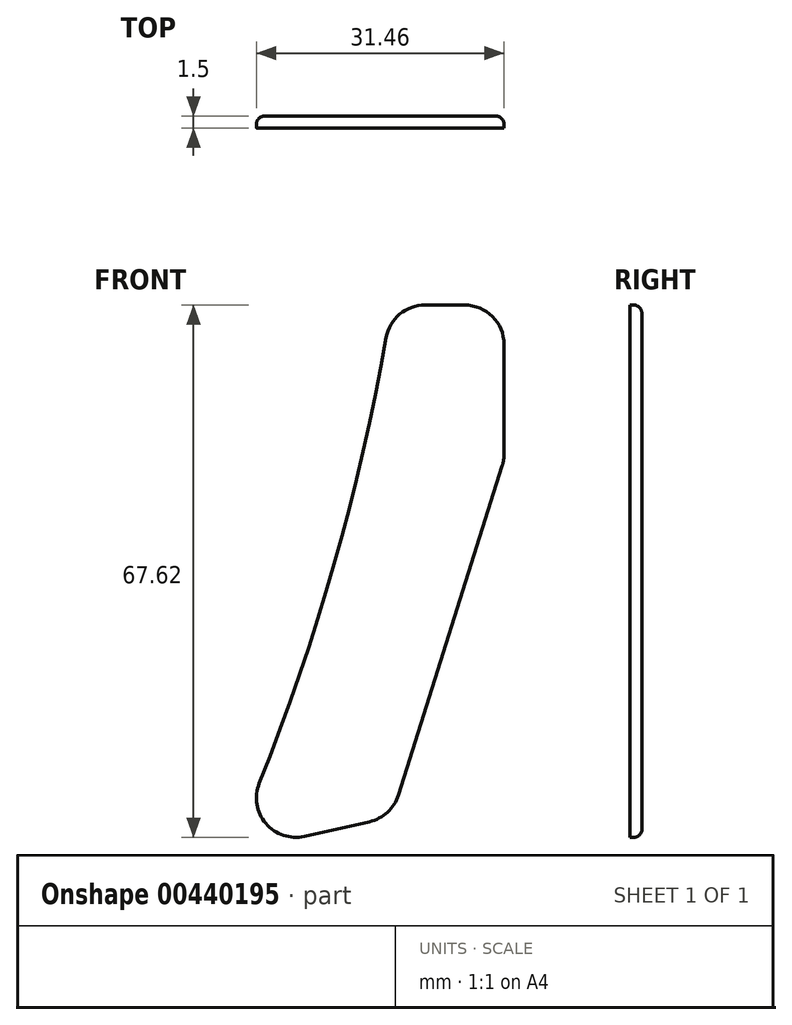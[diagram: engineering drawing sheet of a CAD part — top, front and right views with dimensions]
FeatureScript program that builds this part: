
annotation { "Feature Type Name" : "Feature", "Feature Type Description" : "" }
export const myFeature = defineFeature(function(context is Context, id is Id, definition is map)
    precondition{}
    {
        {
            var Q0;
            Q0=qCreatedBy(makeId("Front.planeOp"),FACE);
            var sketch = newSketch(context, id + "F0", { "sketchPlane" : qUnion([Q0])});
            skLineSegment(sketch, "E0", {"start": v(0, 0) * mm, "end": v(14.28, 0) * mm});
            skLineSegment(sketch, "E1", {"start": v(14.28, 0) * mm, "end": v(14.28, -19.7) * mm});
            skLineSegment(sketch, "E2", {"start": v(14.28, -19.7) * mm, "end": v(0, -65) * mm});
            skLineSegment(sketch, "E3", {"start": v(0, -65) * mm, "end": v(-20.55, -69.63) * mm});
            skLineSegment(sketch, "E4", {"start": v(-20.55, -69.63) * mm, "end": v(-0.94, -2.41) * mm});
            skArc(sketch, "E5", {"start": v(-20.55, -69.63) * mm, "mid": v(-8.05, -35.47) * mm, "end": v(0, 0) * mm});
            skPoint(sketch, "E5.midSnap0", {"position": v(7.14, -42.35) * mm});
            skPoint(sketch, "E5.midSnap1", {"position": v(-10.74, -36.02) * mm});
            skSolve(sketch);
        }
        {
            var Q0;
            Q0 = qSketchRegion(id + "F0", true);
            extrude(context, id + "F1", {"entities" : qUnion([Q0]), "depth" : 1.5 * mm});
        }
        {
            var Q0;
            Q0=makeQuery(id+"F1.opExtrude","SWEPT_EDGE",EDGE,{"disambiguationData":[OSD([sQuery(id+"F0.wireOp",EDGE,"E3"),sQuery(id+"F0.wireOp",EDGE,"E5")])]});
            var Q1;
            Q1=makeQuery(id+"F1.opExtrude","SWEPT_EDGE",EDGE,{"disambiguationData":[OSD([sQuery(id+"F0.wireOp",EDGE,"E2"),sQuery(id+"F0.wireOp",EDGE,"E3")])]});
            var Q2;
            Q2=makeQuery(id+"F1.opExtrude","SWEPT_EDGE",EDGE,{"disambiguationData":[OSD([sQuery(id+"F0.wireOp",EDGE,"E1"),sQuery(id+"F0.wireOp",EDGE,"E2")])]});
            var Q3;
            Q3=makeQuery(id+"F1.opExtrude","SWEPT_EDGE",EDGE,{"disambiguationData":[OSD([sQuery(id+"F0.wireOp",EDGE,"E0"),sQuery(id+"F0.wireOp",EDGE,"E1")])]});
            var Q4;
            Q4=makeQuery(id+"F1.opExtrude","SWEPT_EDGE",EDGE,{"disambiguationData":[OSD([sQuery(id+"F0.wireOp",EDGE,"E0"),sQuery(id+"F0.wireOp",EDGE,"E5")])]});
            fillet(context, id + "F2", {"entities" : qUnion([Q0, Q1, Q2, Q3, Q4]), "radius" : 5 * mm, "tangentPropagation" : true, "allowEdgeOverflow" : false});
        }
        {
            var Q0;
            Q0=makeQuery(id+"F1.opExtrude","CAP_EDGE",EDGE,{"disambiguationData":[OSD([sQuery(id+"F0.wireOp",EDGE,"E5")])],"isStart":true});
            fillet(context, id + "F3", {"entities" : qUnion([Q0]), "radius" : 1 * mm, "tangentPropagation" : true, "allowEdgeOverflow" : false});
        }
    });
